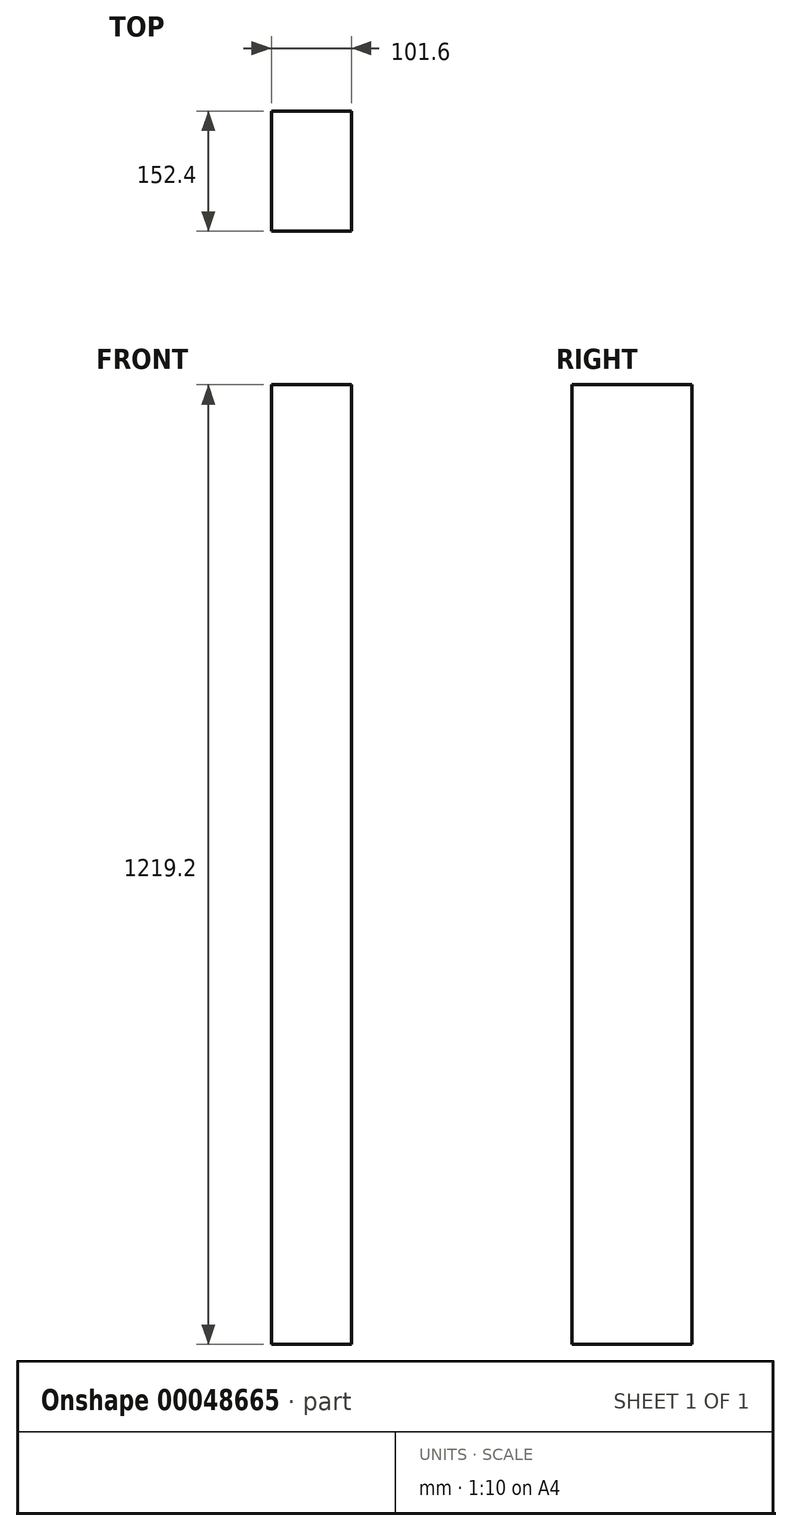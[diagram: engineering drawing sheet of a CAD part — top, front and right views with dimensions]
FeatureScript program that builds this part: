
annotation { "Feature Type Name" : "Feature", "Feature Type Description" : "" }
export const myFeature = defineFeature(function(context is Context, id is Id, definition is map)
    precondition{}
    {
        {
            var Q0;
            Q0=qCreatedBy(makeId("Top.planeOp"),FACE);
            var sketch = newSketch(context, id + "F0", { "sketchPlane" : qUnion([Q0])});
            skLineSegment(sketch, "E0.bottom", {"start": v(0, 0) * mm, "end": v(101.6, 0) * mm});
            skLineSegment(sketch, "E0.top", {"start": v(0, 152.4) * mm, "end": v(101.6, 152.4) * mm});
            skLineSegment(sketch, "E0.left", {"start": v(0, 0) * mm, "end": v(0, 152.4) * mm});
            skLineSegment(sketch, "E0.right", {"start": v(101.6, 0) * mm, "end": v(101.6, 152.4) * mm});
            skSolve(sketch);
        }
        {
            var Q0;
            Q0 = qSketchRegion(id + "F0", true);
            extrude(context, id + "F1", {"entities" : qUnion([Q0]), "depth" : 1219.2 * mm});
        }
    });
